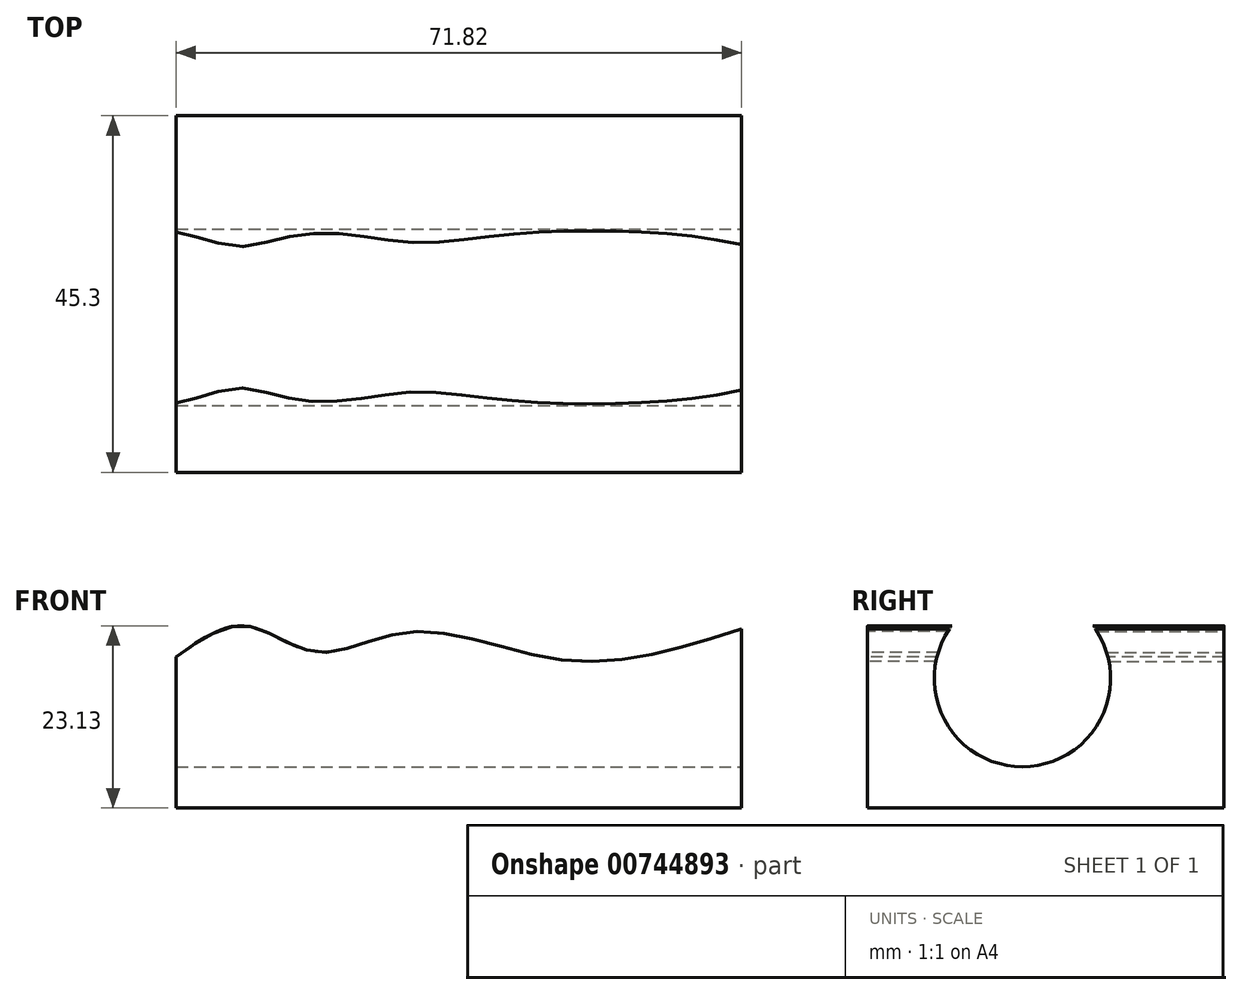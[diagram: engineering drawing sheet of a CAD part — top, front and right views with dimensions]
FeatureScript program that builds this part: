
annotation { "Feature Type Name" : "Feature", "Feature Type Description" : "" }
export const myFeature = defineFeature(function(context is Context, id is Id, definition is map)
    precondition{}
    {
        {
            var Q0;
            Q0=qCreatedBy(makeId("Top.planeOp"),FACE);
            var sketch = newSketch(context, id + "F0", { "sketchPlane" : qUnion([Q0])});
            skLineSegment(sketch, "E0.bottom", {"start": v(-40.7, 23.57) * mm, "end": v(31.12, 23.57) * mm});
            skLineSegment(sketch, "E0.top", {"start": v(-40.7, -21.73) * mm, "end": v(31.12, -21.73) * mm});
            skLineSegment(sketch, "E0.left", {"start": v(-40.7, 23.57) * mm, "end": v(-40.7, -21.73) * mm});
            skLineSegment(sketch, "E0.right", {"start": v(31.12, 23.57) * mm, "end": v(31.12, -21.73) * mm});
            skSolve(sketch);
        }
        {
            var Q0;
            Q0=makeQuery(id+"F0.imprint","IMPRINT",FACE,{"disambiguationData":[TD([[makeQuery(id+"F0.imprint","IMPRINT",EDGE,{"derivedFrom":sQuery(id+"F0.wireOp",EDGE,"E0.bottom")}),-1.0]])]});
            extrude(context, id + "F1", {"entities" : qUnion([Q0]), "depth" : 25 * mm, "offsetDistance" : 25 * mm});
        }
        {
            var Q0;
            Q0=makeQuery(id+"F1.opExtrude","SWEPT_FACE",FACE,{"disambiguationData":[OSD([sQuery(id+"F0.wireOp",EDGE,"E0.right")])]});
            var sketch = newSketch(context, id + "F2", { "sketchPlane" : qUnion([Q0])});
            skCircle(sketch, "E1", {"center": v(-2.05, 16.42) * mm, "radius": 11.2 * mm});
            skSolve(sketch);
        }
        {
            var Q0;
            {var subQ0=sQuery(id+"F2.wireOp",EDGE,"E1");var subQ1=makeQuery(id+"F1.opExtrude","CAP_EDGE",EDGE,{"disambiguationData":[OSD([sQuery(id+"F0.wireOp",EDGE,"E0.right")])],"isStart":false});var subQ2=makeQuery(id+"F2.imprint","INTERSECT",VERTEX,{"disambiguationData":[OD(0.0)],"derivedFrom":[subQ1,subQ0]});Q0=makeQuery(id+"F2.imprint","IMPRINT",FACE,{"disambiguationData":[TD([[makeQuery(id+"F2.imprint","IMPRINT",EDGE,{"disambiguationData":[TD([[subQ2,1.0]])],"derivedFrom":subQ0}),1.0]])]});}
            var Q1;
            Q1=sQuery(id+"F2.wireOp",EDGE,"E1");
            extrude(context, id + "F3", {"entities" : qUnion([Q0]), "operationType" : NewBodyOperationType.REMOVE, "surfaceEntities" : qUnion([Q1]), "endBound" : BoundingType.THROUGH_ALL, "oppositeDirection" : true, "depth" : 25 * mm, "offsetDistance" : 25 * mm});
        }
        {
            var Q0;
            Q0=makeQuery(id+"F1.opExtrude","SWEPT_FACE",FACE,{"disambiguationData":[OSD([sQuery(id+"F0.wireOp",EDGE,"E0.top")])]});
            var sketch = newSketch(context, id + "F4", { "sketchPlane" : qUnion([Q0])});
            skFitSpline(sketch, "E2", {"points": [v(-40.7, 19.15) * mm, v(-31.87, 23.1) * mm, v(-22.78, 19.75) * mm, v(-10.69, 22.39) * mm, v(9.42, 18.68) * mm, v(31.12, 22.72) * mm], "startDerivative": vector(53.74, 38.82) * mm, "endDerivative": vector(87.24, 26.89) * mm});
            skLineSegment(sketch, "E3", {"start": v(-40.7, 19.15) * mm, "end": v(-40.7, 25) * mm});
            skLineSegment(sketch, "E4", {"start": v(-40.7, 25) * mm, "end": v(31.12, 25) * mm});
            skLineSegment(sketch, "E5", {"start": v(31.12, 25) * mm, "end": v(31.12, 22.72) * mm});
            skSolve(sketch);
        }
        {
            var Q0;
            Q0=makeQuery(id+"F4.imprint","IMPRINT",FACE,{"disambiguationData":[TD([[makeQuery(id+"F4.imprint","IMPRINT",EDGE,{"derivedFrom":sQuery(id+"F4.wireOp",EDGE,"E2")}),1.0]])]});
            extrude(context, id + "F5", {"entities" : qUnion([Q0]), "operationType" : NewBodyOperationType.REMOVE, "endBound" : BoundingType.THROUGH_ALL, "oppositeDirection" : true, "depth" : 25 * mm, "offsetDistance" : 25 * mm});
        }
    });
